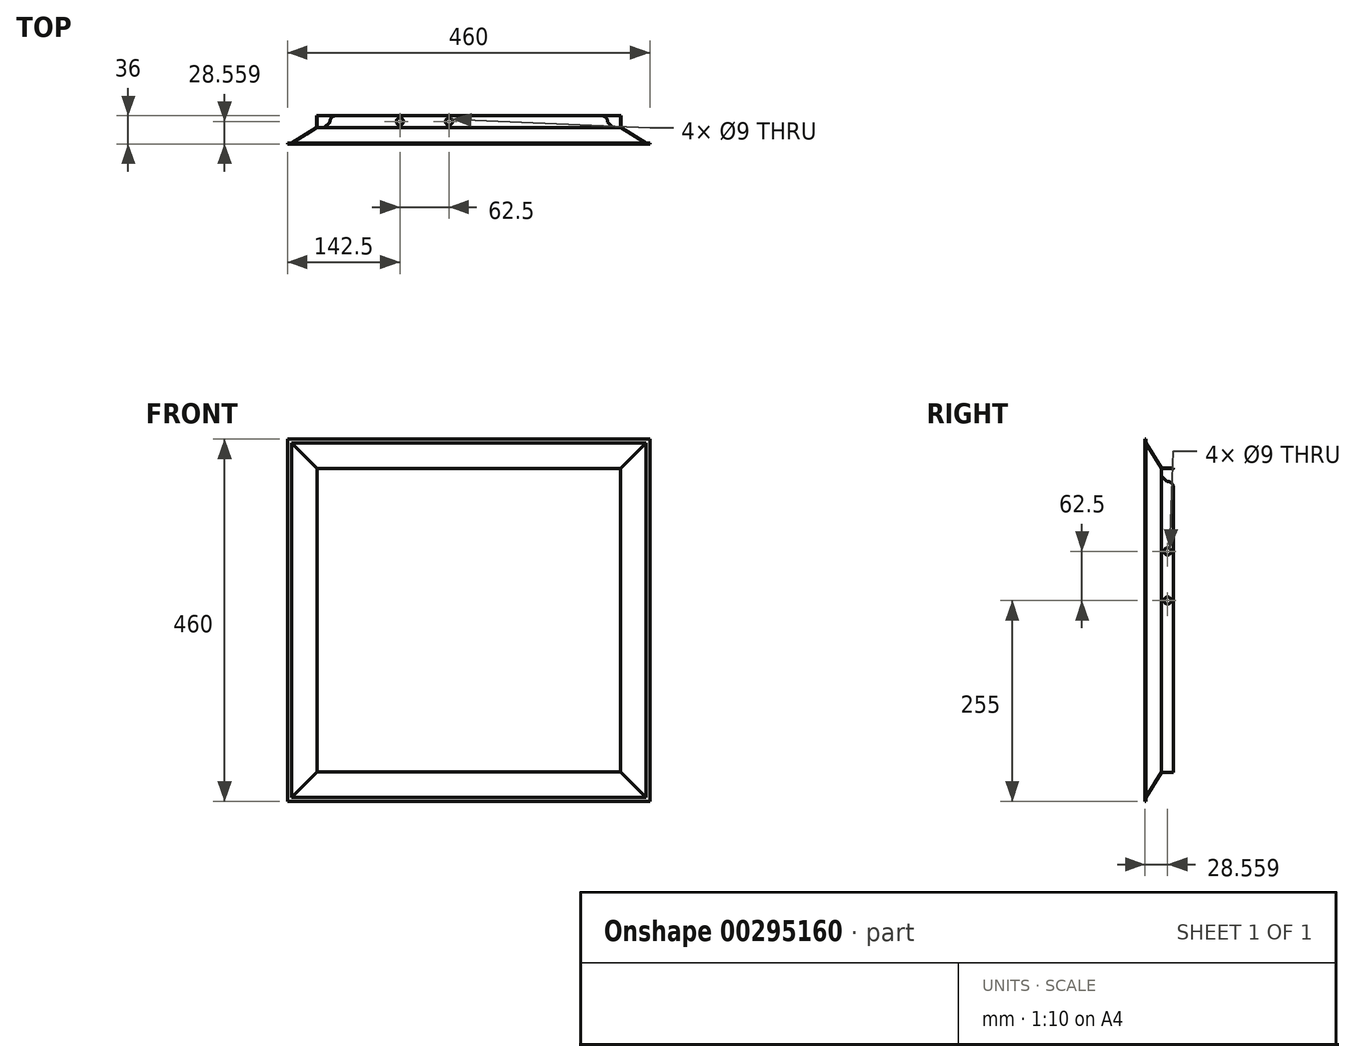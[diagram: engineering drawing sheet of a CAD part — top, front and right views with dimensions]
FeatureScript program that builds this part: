
annotation { "Feature Type Name" : "Feature", "Feature Type Description" : "" }
export const myFeature = defineFeature(function(context is Context, id is Id, definition is map)
    precondition{}
    {
        {
            var Q0;
            Q0=qCreatedBy(makeId("Front.planeOp"),FACE);
            var sketch = newSketch(context, id + "F0", { "sketchPlane" : qUnion([Q0])});
            skLineSegment(sketch, "E0.bottom", {"start": v(230, 230) * mm, "end": v(-230, 230) * mm});
            skLineSegment(sketch, "E0.top", {"start": v(230, -230) * mm, "end": v(-230, -230) * mm});
            skLineSegment(sketch, "E0.left", {"start": v(230, 230) * mm, "end": v(230, -230) * mm});
            skLineSegment(sketch, "E0.right", {"start": v(-230, 230) * mm, "end": v(-230, -230) * mm});
            skPoint(sketch, "E0.middle", {"position": v(0, 0) * mm});
            skLineSegment(sketch, "E1.0", {"start": v(225, 225) * mm, "end": v(-225, 225) * mm});
            skLineSegment(sketch, "E1.1", {"start": v(225, 225) * mm, "end": v(225, -225) * mm});
            skLineSegment(sketch, "E1.2", {"start": v(225, -225) * mm, "end": v(-225, -225) * mm});
            skLineSegment(sketch, "E1.3", {"start": v(-225, 225) * mm, "end": v(-225, -225) * mm});
            skSolve(sketch);
        }
        {
            var Q0;
            Q0=makeQuery(id+"F0.imprint","IMPRINT",FACE,{"disambiguationData":[TD([[makeQuery(id+"F0.imprint","IMPRINT",EDGE,{"derivedFrom":sQuery(id+"F0.wireOp",EDGE,"E1.0")}),1.0]])]});
            cPlane(context, id + "F1", {"entities" : qUnion([Q0]), "cplaneType" : CPlaneType.OFFSET, "offset" : 20 * mm, "oppositeDirection" : true, "width" : 150 * mm, "height" : 150 * mm});
        }
        {
            var Q0;
            Q0=qCreatedBy(id+"F1.planeOp",FACE);
            var sketch = newSketch(context, id + "F2", { "sketchPlane" : qUnion([Q0])});
            skPoint(sketch, "E2", {"position": v(0, 0) * mm});
            skLineSegment(sketch, "E3.bottom", {"start": v(192.5, 192.5) * mm, "end": v(-192.5, 192.5) * mm});
            skLineSegment(sketch, "E3.top", {"start": v(192.5, -192.5) * mm, "end": v(-192.5, -192.5) * mm});
            skLineSegment(sketch, "E3.left", {"start": v(192.5, 192.5) * mm, "end": v(192.5, -192.5) * mm});
            skLineSegment(sketch, "E3.right", {"start": v(-192.5, 192.5) * mm, "end": v(-192.5, -192.5) * mm});
            skSolve(sketch);
        }
        {
            var Q0;
            Q0=qCreatedBy(id+"F1.planeOp",FACE);
            cPlane(context, id + "F3", {"entities" : qUnion([Q0]), "cplaneType" : CPlaneType.OFFSET, "offset" : 16 * mm, "oppositeDirection" : true, "width" : 150 * mm, "height" : 150 * mm});
        }
        {
            var Q0;
            Q0=qCreatedBy(id+"F3.planeOp",FACE);
            var sketch = newSketch(context, id + "F4", { "sketchPlane" : qUnion([Q0])});
            skLineSegment(sketch, "E4.0.0", {"start": v(-192.5, -192.5) * mm, "end": v(192.5, -192.5) * mm});
            skLineSegment(sketch, "E4.0.1", {"start": v(192.5, -192.5) * mm, "end": v(192.5, 192.5) * mm});
            skLineSegment(sketch, "E4.0.2", {"start": v(192.5, 192.5) * mm, "end": v(-192.5, 192.5) * mm});
            skLineSegment(sketch, "E4.0.3", {"start": v(-192.5, 192.5) * mm, "end": v(-192.5, -192.5) * mm});
            skSolve(sketch);
        }
        {
            var Q0;
            Q0=makeQuery(id+"F0.imprint","IMPRINT",FACE,{"disambiguationData":[TD([[makeQuery(id+"F0.imprint","IMPRINT",EDGE,{"derivedFrom":sQuery(id+"F0.wireOp",EDGE,"E1.0")}),1.0]])]});
            var Q1;
            Q1=makeQuery(id+"F2.imprint","IMPRINT",FACE,{"disambiguationData":[TD([[makeQuery(id+"F2.imprint","IMPRINT",EDGE,{"derivedFrom":sQuery(id+"F2.wireOp",EDGE,"E3.bottom")}),1.0]])]});
            loft(context, id + "F5", {"sheetProfilesArray" : [{ "sheetProfileEntities" : qUnion([Q0]) }, { "sheetProfileEntities" : qUnion([Q1]) }]});
        }
        {
            var Q1;
            Q1=makeQuery(id+"F2.imprint","IMPRINT",FACE,{"disambiguationData":[TD([[makeQuery(id+"F2.imprint","IMPRINT",EDGE,{"derivedFrom":sQuery(id+"F2.wireOp",EDGE,"E3.bottom")}),1.0]])]});
            var Q2;
            Q2=makeQuery(id+"F4.imprint","IMPRINT",FACE,{"disambiguationData":[TD([[makeQuery(id+"F4.imprint","IMPRINT",EDGE,{"derivedFrom":sQuery(id+"F4.wireOp",EDGE,"E4.0.0")}),1.0]])]});
            loft(context, id + "F6", {"operationType" : NewBodyOperationType.ADD, "sheetProfilesArray" : [{ "sheetProfileEntities" : qUnion([Q1]) }, { "sheetProfileEntities" : qUnion([Q2]) }]});
        }
        {
            var Q0;
            Q0=makeQuery(id+"F5.opLoft","CAP_FACE",FACE,{"disambiguationData":[OSD([makeQuery(id+"F0.imprint","IMPRINT",FACE,{"disambiguationData":[TD([[makeQuery(id+"F0.imprint","IMPRINT",EDGE,{"derivedFrom":sQuery(id+"F0.wireOp",EDGE,"E1.0")}),1.0]])]})])],"isStart":true});
            var Q1;
            Q1=makeQuery(id+"F6.opLoft","CAP_FACE",FACE,{"disambiguationData":[OSD([makeQuery(id+"F4.imprint","IMPRINT",FACE,{"disambiguationData":[TD([[makeQuery(id+"F4.imprint","IMPRINT",EDGE,{"derivedFrom":sQuery(id+"F4.wireOp",EDGE,"E4.0.0")}),1.0]])]})])],"isStart":true});
            shell(context, id + "F7", {"entities" : qUnion([Q0, Q1]), "thickness" : 1 * mm, "oppositeDirection" : true});
        }
        {
            var Q0;
            Q0=makeQuery(id+"F0.imprint","IMPRINT",FACE,{"disambiguationData":[TD([[makeQuery(id+"F0.imprint","IMPRINT",EDGE,{"derivedFrom":sQuery(id+"F0.wireOp",EDGE,"E0.bottom")}),1.0]])]});
            extrude(context, id + "F8", {"entities" : qUnion([Q0]), "operationType" : NewBodyOperationType.ADD, "oppositeDirection" : true, "depth" : 1 * mm});
        }
        {
            var Q0;
            Q0=makeQuery(id+"F6.opLoft","SWEPT_FACE",FACE,{"disambiguationData":[OSD([sQuery(id+"F2.wireOp",EDGE,"E3.bottom"),sQuery(id+"F2.wireOp",EDGE,"E3.left"),sQuery(id+"F2.wireOp",EDGE,"E3.right"),sQuery(id+"F4.wireOp",EDGE,"E4.0.1"),sQuery(id+"F4.wireOp",EDGE,"E4.0.2"),sQuery(id+"F4.wireOp",EDGE,"E4.0.3")])]});
            var sketch = newSketch(context, id + "F9", { "sketchPlane" : qUnion([Q0])});
            skLineSegment(sketch, "E5", {"start": v(-193.5, 20.56) * mm, "end": v(-183.5, 20.56) * mm});
            skLineSegment(sketch, "E6", {"start": v(-183.5, 20.56) * mm, "end": v(-176.43, 27.63) * mm});
            skArc(sketch, "E7", {"start": v(-168.43, 36) * mm, "mid": v(-174.22, 33.53) * mm, "end": v(-176.43, 27.63) * mm});
            skLineSegment(sketch, "E8", {"start": v(-168.43, 36) * mm, "end": v(-196.47, 36) * mm});
            skLineSegment(sketch, "E9", {"start": v(-196.47, 36) * mm, "end": v(-196.47, 20.56) * mm});
            skLineSegment(sketch, "E10", {"start": v(-196.47, 20.56) * mm, "end": v(-193.5, 20.56) * mm});
            skLineSegment(sketch, "E11.MirrorCS", {"start": v(196.47, 20.56) * mm, "end": v(193.5, 20.56) * mm});
            skLineSegment(sketch, "E12.MirrorCS", {"start": v(193.5, 20.56) * mm, "end": v(183.5, 20.56) * mm});
            skLineSegment(sketch, "E13.MirrorCS", {"start": v(183.5, 20.56) * mm, "end": v(176.43, 27.63) * mm});
            skLineSegment(sketch, "E14.MirrorCS", {"start": v(168.43, 36) * mm, "end": v(196.47, 36) * mm});
            skLineSegment(sketch, "E15.MirrorCS", {"start": v(196.47, 36) * mm, "end": v(196.47, 20.56) * mm});
            skArc(sketch, "E16.MirrorCS", {"start": v(168.43, 36) * mm, "mid": v(174.22, 33.53) * mm, "end": v(176.43, 27.63) * mm});
            skLineSegment(sketch, "E17", {"start": v(-193.5, 20.56) * mm, "end": v(-193.5, 36) * mm});
            skLineSegment(sketch, "E18.MirrorCS", {"start": v(193.5, 20.56) * mm, "end": v(193.5, 36) * mm});
            skSolve(sketch);
        }
        {
            var Q0;
            Q0=makeQuery(id+"F9.imprint","IMPRINT",FACE,{"disambiguationData":[TD([[makeQuery(id+"F9.imprint","IMPRINT",EDGE,{"derivedFrom":sQuery(id+"F9.wireOp",EDGE,"E5")}),1.0]])]});
            var Q1;
            Q1=sQuery(id+"F9.wireOp",EDGE,"E17");
            revolve(context, id + "F10", {"operationType" : NewBodyOperationType.REMOVE, "entities" : qUnion([Q0]), "axis" : qUnion([Q1]), "revolveType" : RevolveType.FULL, "oppositeDirection" : true});
        }
        {
            var Q0;
            Q0=makeQuery(id+"F9.imprint","IMPRINT",FACE,{"disambiguationData":[TD([[makeQuery(id+"F9.imprint","IMPRINT",EDGE,{"derivedFrom":sQuery(id+"F9.wireOp",EDGE,"E12.MirrorCS")}),1.0]])]});
            var Q1;
            Q1=sQuery(id+"F9.wireOp",EDGE,"E18.MirrorCS");
            revolve(context, id + "F11", {"operationType" : NewBodyOperationType.REMOVE, "entities" : qUnion([Q0]), "axis" : qUnion([Q1]), "revolveType" : RevolveType.FULL, "oppositeDirection" : true});
        }
        {
            var Q0;
            Q0=qCreatedBy(makeId("Top.planeOp"),FACE);
            var sketch = newSketch(context, id + "F12", { "sketchPlane" : qUnion([Q0])});
            skCircle(sketch, "E19", {"center": v(-25, 28.56) * mm, "radius": 4.5 * mm});
            skCircle(sketch, "E20", {"center": v(-87.5, 28.56) * mm, "radius": 4.5 * mm});
            skLineSegment(sketch, "E21", {"start": v(0, -35.8) * mm, "end": v(0, 97.38) * mm, "construction": true});
            skCircle(sketch, "E22.MirrorC", {"center": v(25, 28.56) * mm, "radius": 4.5 * mm});
            skCircle(sketch, "E23.MirrorC", {"center": v(87.5, 28.56) * mm, "radius": 4.5 * mm});
            skSolve(sketch);
        }
        {
            var Q0;
            Q0=makeQuery(id+"F12.imprint","IMPRINT",FACE,{"disambiguationData":[TD([[makeQuery(id+"F12.imprint","IMPRINT",EDGE,{"derivedFrom":sQuery(id+"F12.wireOp",EDGE,"E23.MirrorC")}),-1.0]])]});
            var Q1;
            Q1=makeQuery(id+"F12.imprint","IMPRINT",FACE,{"disambiguationData":[TD([[makeQuery(id+"F12.imprint","IMPRINT",EDGE,{"derivedFrom":sQuery(id+"F12.wireOp",EDGE,"E22.MirrorC")}),-1.0]])]});
            var Q2;
            Q2=makeQuery(id+"F12.imprint","IMPRINT",FACE,{"disambiguationData":[TD([[makeQuery(id+"F12.imprint","IMPRINT",EDGE,{"derivedFrom":sQuery(id+"F12.wireOp",EDGE,"E19")}),1.0]])]});
            var Q3;
            Q3=makeQuery(id+"F12.imprint","IMPRINT",FACE,{"disambiguationData":[TD([[makeQuery(id+"F12.imprint","IMPRINT",EDGE,{"derivedFrom":sQuery(id+"F12.wireOp",EDGE,"E20")}),1.0]])]});
            extrude(context, id + "F13", {"entities" : qUnion([Q0, Q1, Q2, Q3]), "operationType" : NewBodyOperationType.REMOVE, "endBound" : BoundingType.SYMMETRIC, "oppositeDirection" : true, "depth" : 766 * mm});
        }
        {
            var Q0;
            Q0=qCreatedBy(makeId("Right.planeOp"),FACE);
            var sketch = newSketch(context, id + "F14", { "sketchPlane" : qUnion([Q0])});
            skCircle(sketch, "E24", {"center": v(28.56, 25) * mm, "radius": 4.5 * mm});
            skCircle(sketch, "E25", {"center": v(28.56, 87.5) * mm, "radius": 4.5 * mm});
            skLineSegment(sketch, "E26", {"start": v(-22.7, 0) * mm, "end": v(43.68, 0) * mm, "construction": true});
            skCircle(sketch, "E27.MirrorC", {"center": v(28.56, -25) * mm, "radius": 4.5 * mm});
            skCircle(sketch, "E28.MirrorC", {"center": v(28.56, -87.5) * mm, "radius": 4.5 * mm});
            skSolve(sketch);
        }
        {
            var Q0;
            Q0=makeQuery(id+"F14.imprint","IMPRINT",FACE,{"disambiguationData":[TD([[makeQuery(id+"F14.imprint","IMPRINT",EDGE,{"derivedFrom":sQuery(id+"F14.wireOp",EDGE,"E28.MirrorC")}),-1.0]])]});
            var Q1;
            Q1=makeQuery(id+"F14.imprint","IMPRINT",FACE,{"disambiguationData":[TD([[makeQuery(id+"F14.imprint","IMPRINT",EDGE,{"derivedFrom":sQuery(id+"F14.wireOp",EDGE,"E27.MirrorC")}),-1.0]])]});
            var Q2;
            Q2=makeQuery(id+"F14.imprint","IMPRINT",FACE,{"disambiguationData":[TD([[makeQuery(id+"F14.imprint","IMPRINT",EDGE,{"derivedFrom":sQuery(id+"F14.wireOp",EDGE,"E24")}),1.0]])]});
            var Q3;
            Q3=makeQuery(id+"F14.imprint","IMPRINT",FACE,{"disambiguationData":[TD([[makeQuery(id+"F14.imprint","IMPRINT",EDGE,{"derivedFrom":sQuery(id+"F14.wireOp",EDGE,"E25")}),1.0]])]});
            extrude(context, id + "F15", {"entities" : qUnion([Q0, Q1, Q2, Q3]), "operationType" : NewBodyOperationType.REMOVE, "endBound" : BoundingType.SYMMETRIC, "oppositeDirection" : true, "depth" : 456 * mm});
        }
    });
